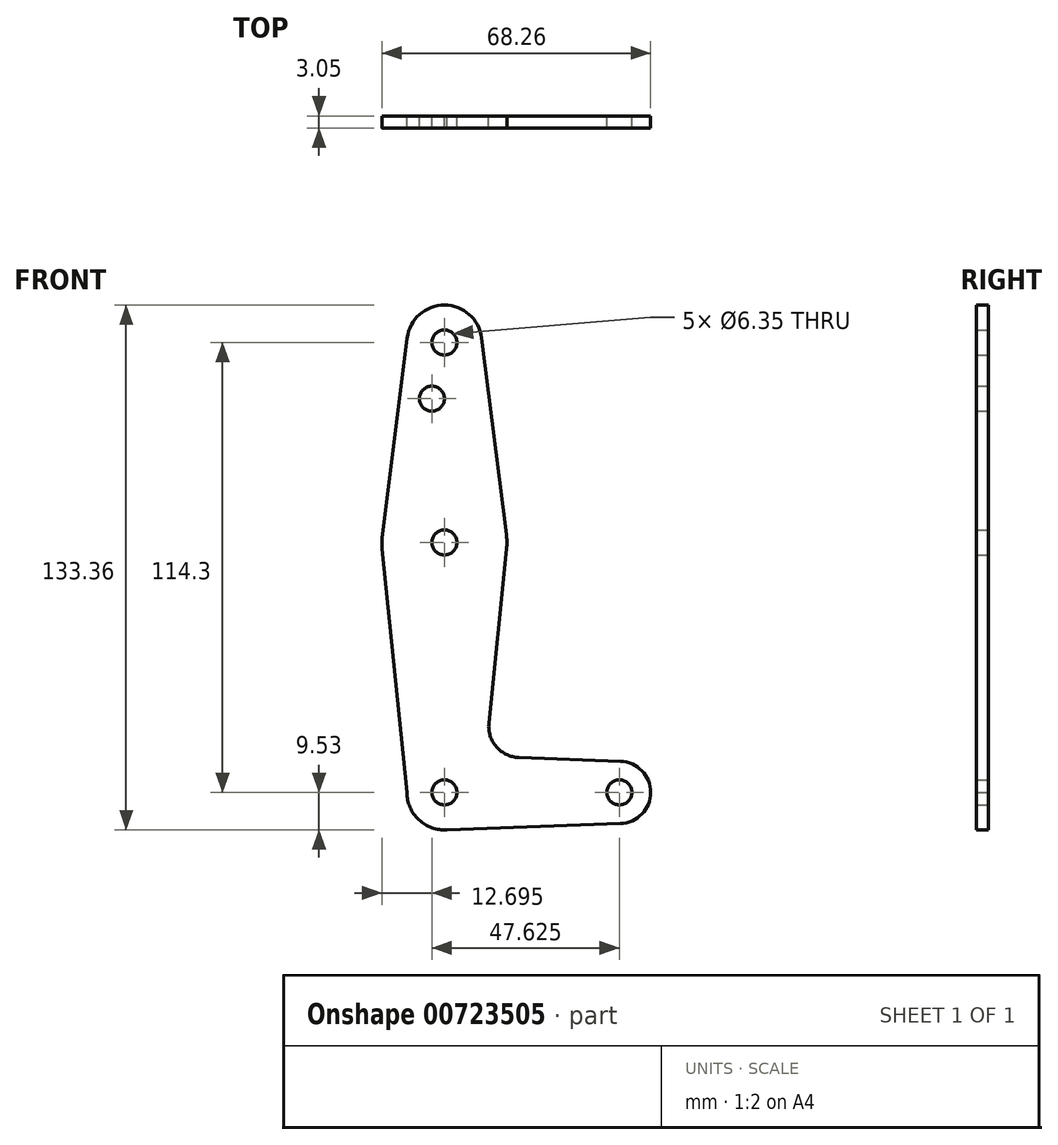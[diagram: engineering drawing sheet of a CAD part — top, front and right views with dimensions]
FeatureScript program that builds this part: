
annotation { "Feature Type Name" : "Feature", "Feature Type Description" : "" }
export const myFeature = defineFeature(function(context is Context, id is Id, definition is map)
    precondition{}
    {
        {
            var Q0;
            Q0=qCreatedBy(makeId("Front.planeOp"),FACE);
            var sketch = newSketch(context, id + "F0", { "sketchPlane" : qUnion([Q0])});
            skLineSegment(sketch, "E0", {"start": v(0, 0) * mm, "end": v(0, 114.3) * mm, "construction": true});
            skLineSegment(sketch, "E1", {"start": v(0, 0) * mm, "end": v(44.45, 0) * mm, "construction": true});
            skCircle(sketch, "E2", {"center": v(44.45, 0) * mm, "radius": 7.94 * mm});
            skCircle(sketch, "E3", {"center": v(0, 0) * mm, "radius": 9.53 * mm});
            skCircle(sketch, "E4", {"center": v(0, 114.3) * mm, "radius": 9.53 * mm});
            skCircle(sketch, "E5", {"center": v(0, 63.5) * mm, "radius": 15.88 * mm});
            skLineSegment(sketch, "E6", {"start": v(18.93, 8.85) * mm, "end": v(44.73, 7.93) * mm});
            skLineSegment(sketch, "E7", {"start": v(0, -9.53) * mm, "end": v(44.73, -7.93) * mm});
            skLineSegment(sketch, "E8", {"start": v(-9.45, 115.5) * mm, "end": v(-15.75, 65.48) * mm});
            skLineSegment(sketch, "E9", {"start": v(9.45, 115.5) * mm, "end": v(15.75, 65.48) * mm});
            skLineSegment(sketch, "E10", {"start": v(-9.53, 0) * mm, "end": v(-15.8, 61.9) * mm});
            skPoint(sketch, "E10.startSnap0", {"position": v(22.23, 0) * mm});
            skLineSegment(sketch, "E11", {"start": v(11.3, 17.6) * mm, "end": v(15.8, 61.9) * mm});
            skCircle(sketch, "E12", {"center": v(0, 0) * mm, "radius": 3.18 * mm});
            skCircle(sketch, "E13", {"center": v(0, 114.3) * mm, "radius": 3.18 * mm});
            skCircle(sketch, "E14", {"center": v(0, 63.5) * mm, "radius": 3.18 * mm});
            skCircle(sketch, "E15", {"center": v(44.45, 0) * mm, "radius": 3.18 * mm});
            skCircle(sketch, "E16", {"center": v(-3.18, 100.03) * mm, "radius": 3.18 * mm});
            skArc(sketch, "E17.filletArc", {"start": v(11.3, 17.6) * mm, "mid": v(13.22, 11.57) * mm, "end": v(18.93, 8.85) * mm});
            skSolve(sketch);
        }
        {
            var Q0;
            Q0 = qSketchRegion(id + "F0", true);
            extrude(context, id + "F1", {"entities" : qUnion([Q0]), "depth" : 3.05 * mm, "offsetDistance" : 25.4 * mm});
        }
    });
